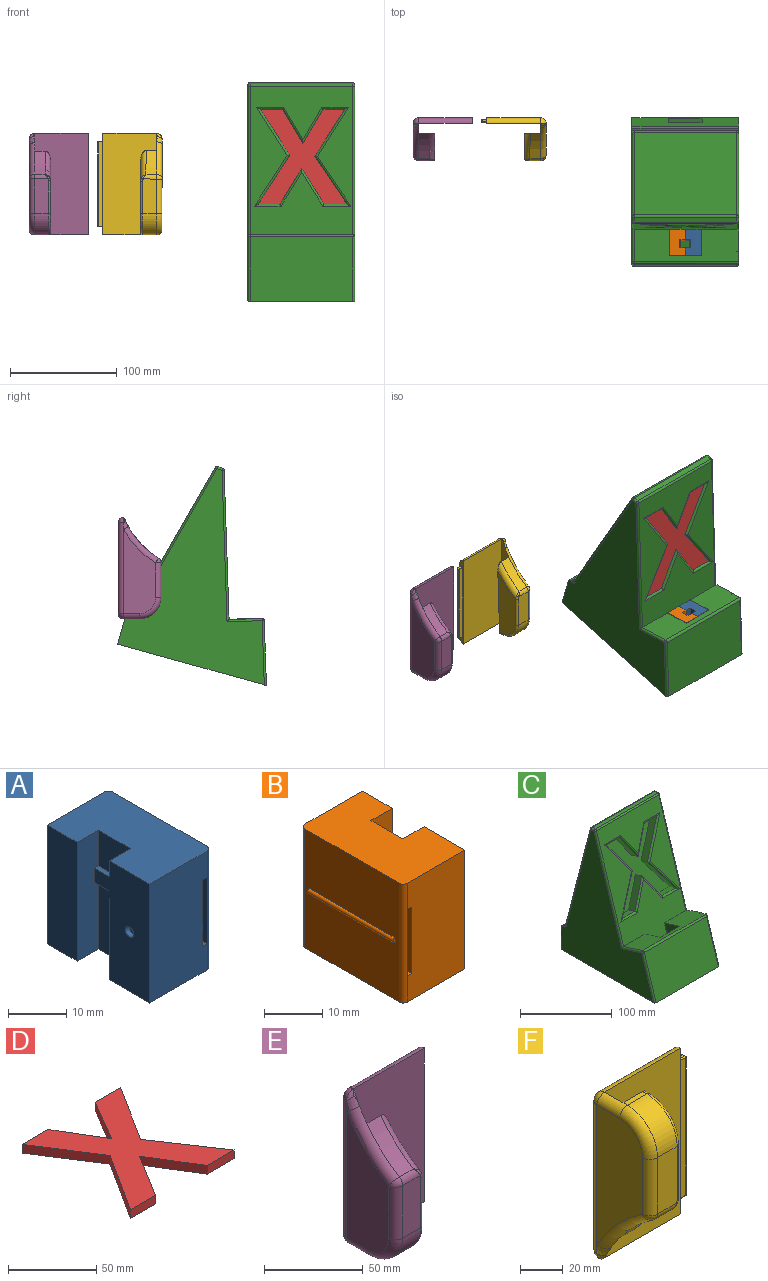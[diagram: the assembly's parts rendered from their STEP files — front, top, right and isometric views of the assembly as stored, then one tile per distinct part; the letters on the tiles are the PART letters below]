
ASSEMBLY  parts=6 mates=4
PART A: 25 faces, bbox 15.5x24.9x25 mm
  f0: plane 25x22.9mm, normal (1,0,0), area 551.6mm2, adj f6,f7,f20,f21,f22,f23,f24
  f1: plane 25x13.95mm, normal (0,1,0), area 334.7mm2, adj f6,f7,f8,f16,f18,f19,f24
  f2: plane 25x13.95mm, normal (0,-1,0), area 334.7mm2, adj f5,f6,f7,f16,f18,f19,f23
  f3: plane 7.75x7.5mm, normal (-1,0,0), area 58.1mm2, adj f4,f6,f9,f13
  f4: plane 25x5.17mm, normal (0,1,0), area 126.1mm2, adj f3,f5,f6,f7,f10,f13,f14,f15
  f5: plane 25x9.89mm, normal (-1,0,0), area 243.8mm2, adj f2,f4,f6,f7,f11
  f6: plane 24.9x14.95mm, normal (0,0,1), area 331.8mm2, adj f0,f1,f2,f3,f4,f5,f8,f9
  f7: plane 24.9x14.95mm, normal (0,0,-1), area 331.8mm2, adj f0,f1,f2,f4,f5,f8,f9,f10
  f8: plane 25x7.27mm, normal (-1,0,0), area 181.6mm2, adj f1,f6,f7,f9
  f9: plane 25x5.17mm, normal (0,-1,0), area 126.1mm2, adj f3,f6,f7,f8,f10,f13,f14,f15
  f10: plane 14.5x7.75mm, normal (-1,0,0), area 112.4mm2, adj f4,f7,f9,f14
  f11: cylinder r=1.03mm len=2.05mm, axis (-1,0,0), area 6.4mm2, adj f5,f12
  f12: plane 2.05x2.05mm, normal (-1,0,0), area 3.3mm2, adj f11
  f13: plane 7.75x1mm, normal (0,0,1), area 7.7mm2, adj f3,f4,f9,f15
  f14: plane 7.75x1mm, normal (0,0,-1), area 7.7mm2, adj f4,f9,f10,f15
  f15: plane 7.75x3mm, normal (-1,0,0), area 23.3mm2, adj f4,f9,f13,f14
  f16: plane 24.9x1mm, normal (0,0,-1), area 24.9mm2, adj f1,f2,f17,f19
  f17: plane 24.9x14mm, normal (-1,0,0), area 348.6mm2, adj f16,f18,f23,f24
  f18: plane 24.9x1mm, normal (0,0,1), area 24.9mm2, adj f1,f2,f17,f19
  f19: plane 24.9x14mm, normal (1,0,0), area 348.6mm2, adj f1,f2,f16,f18
  f20: plane 1x0.5mm, normal (0,-1,0), area 0.4mm2, adj f0,f21
  f21: cylinder r=0.5mm len=20.9mm, axis (0,1,0), area 32.8mm2, adj f0,f20,f22
  f22: plane 1x0.5mm, normal (0,1,0), area 0.4mm2, adj f0,f21
  f23: cylinder r=1mm len=25mm, axis (0,0,1), area 39.3mm2, adj f0,f2,f6,f7,f17
  f24: cylinder r=1mm len=25mm, axis (0,0,-1), area 39.3mm2, adj f0,f1,f6,f7,f17
PART B: 26 faces, bbox 16.5x24.9x25 mm
  f0: plane 25x13.95mm, normal (0,1,0), area 334.8mm2, adj f5,f6,f7,f18,f19,f20,f24
  f1: plane 25x13.95mm, normal (0,-1,0), area 334.8mm2, adj f4,f5,f6,f18,f19,f20,f25
  f2: plane 14.5x7.75mm, normal (1,0,0), area 112.4mm2, adj f3,f6,f9,f15
  f3: plane 25x5.17mm, normal (0,1,0), area 126.1mm2, adj f2,f4,f5,f6,f10,f14,f15,f16
  f4: plane 25x9.89mm, normal (1,0,0), area 244mm2, adj f1,f3,f5,f6,f11
  f5: plane 24.9x14.95mm, normal (0,0,1), area 331.8mm2, adj f0,f1,f3,f4,f7,f8,f9,f10
  f6: plane 24.9x14.95mm, normal (0,0,-1), area 331.8mm2, adj f0,f1,f2,f3,f4,f7,f8,f9
  f7: plane 25x7.27mm, normal (1,0,0), area 181.6mm2, adj f0,f5,f6,f9
  f8: plane 25x22.9mm, normal (-1,0,0), area 551.6mm2, adj f5,f6,f21,f22,f23,f24,f25
  f9: plane 25x5.17mm, normal (0,-1,0), area 126.1mm2, adj f2,f5,f6,f7,f10,f14,f15,f16
  f10: plane 7.75x7.5mm, normal (1,0,0), area 58.1mm2, adj f3,f5,f9,f14
  f11: cylinder r=1mm len=2mm, axis (-1,0,0), area 0.6mm2, adj f4,f13
  f12: plane 0.2x0.2mm, normal (1,0,0), area 0mm2, adj f13
  f13: torus R=0.1mm, axis (1,0,0), area 6mm2, adj f11,f12
  f14: plane 7.75x1mm, normal (0,0,1), area 7.8mm2, adj f3,f9,f10,f16
  f15: plane 7.75x1mm, normal (0,0,-1), area 7.8mm2, adj f2,f3,f9,f16
  f16: plane 7.75x3mm, normal (1,0,0), area 23.3mm2, adj f3,f9,f14,f15
  f17: plane 24.9x14mm, normal (1,0,0), area 348.6mm2, adj f18,f20,f24,f25
  f18: plane 24.9x1mm, normal (0,0,-1), area 24.9mm2, adj f0,f1,f17,f19
  f19: plane 24.9x14mm, normal (-1,0,0), area 348.6mm2, adj f0,f1,f18,f20
  f20: plane 24.9x1mm, normal (0,0,1), area 24.9mm2, adj f0,f1,f17,f19
  f21: plane 1x0.5mm, normal (0,-1,0), area 0.4mm2, adj f8,f23
  f22: plane 1x0.5mm, normal (0,1,0), area 0.4mm2, adj f8,f23
  f23: cylinder r=0.5mm len=20.9mm, axis (0,1,0), area 32.8mm2, adj f8,f21,f22
  f24: cylinder r=1mm len=25mm, axis (0,0,-1), area 39.3mm2, adj f0,f5,f6,f8,f17
  f25: cylinder r=1mm len=25mm, axis (0,0,1), area 39.3mm2, adj f1,f5,f6,f8,f17
PART C: 74 faces, bbox 104.8x145.3x186.4 mm
  f0: plane 44.02x37.32mm, normal (1,0,0), area 931.5mm2, adj f6,f9,f54,f58,f61,f62,f71,f72
  f1: plane 44.02x37.32mm, normal (-1,0,0), area 931.5mm2, adj f6,f9,f54,f58,f61,f62,f68,f69
  f2: plane 100x30.22mm, normal (0,1,0), area 2531.6mm2, adj f3,f5,f8,f38,f54,f55,f56,f57
  f3: plane 183.83x143.2mm, normal (-1,0,0), area 12324.4mm2, adj f2,f5,f10,f26,f30,f31,f38,f51
  f4: plane 2.36x2.26mm, normal (0,0,1), area 0.9mm2, adj f8,f25,f59
  f5: plane 144.72x100.26mm, normal (0,0,-1), area 14444.2mm2, adj f2,f3,f8,f60,f63,f67
  f6: plane 165.85x96mm, normal (0,-0.95,0.3), area 10214.6mm2, adj f0,f1,f9,f26,f28,f29,f39,f40
  f7: plane 96x4.78mm, normal (0,0,1), area 459.1mm2, adj f29,f30,f34,f35
  f8: plane 183.83x143.2mm, normal (1,0,0), area 12324.9mm2, adj f2,f4,f5,f9,f10,f25,f28,f34
  f9: plane 98x31.34mm, normal (0,0.3,0.95), area 2272.5mm2, adj f0,f1,f6,f8,f25,f28,f59,f61
  f10: plane 100x2mm, normal (0,0,1), area 145.2mm2, adj f3,f8,f38,f51,f52,f53
  f11: plane 149.78x96mm, normal (0,0.97,0.25), area 14844.8mm2, adj f31,f35,f37,f52
  f12: plane 21.45x9.54mm, normal (0,0.3,0.95), area 214.5mm2, adj f13,f23,f24,f46
  f13: plane 45.62x29.95mm, normal (-0.83,-0.17,-0.53), area 537.8mm2, adj f12,f14,f24,f44
  f14: plane 44.93x27.82mm, normal (-0.85,0.16,0.51), area 520.2mm2, adj f13,f15,f24,f42
  f15: plane 20.23x9.54mm, normal (0,-0.3,-0.95), area 202.3mm2, adj f14,f16,f24,f40
  f16: plane 33.42x19.08mm, normal (0.86,-0.15,-0.48), area 369.9mm2, adj f15,f17,f24,f39
  f17: plane 33.42x19.09mm, normal (-0.86,-0.15,-0.49), area 371.7mm2, adj f16,f18,f24,f41
  f18: plane 20.74x9.54mm, normal (0,-0.3,-0.95), area 207.4mm2, adj f17,f19,f24,f43
  f19: plane 43.95x27.53mm, normal (0.84,0.16,0.52), area 509.9mm2, adj f18,f20,f24,f45
  f20: plane 46.6x29.41mm, normal (0.84,-0.16,-0.52), area 543.5mm2, adj f19,f21,f24,f47
  f21: plane 20.14x9.54mm, normal (0,0.3,0.95), area 201.4mm2, adj f20,f22,f24,f49
  f22: plane 34.98x20.6mm, normal (-0.85,0.16,0.5), area 393.4mm2, adj f21,f23,f24,f50
  f23: plane 34.98x20.62mm, normal (0.85,0.16,0.5), area 393.5mm2, adj f12,f22,f24,f48
  f24: plane 84.57x82.81mm, normal (0,-0.95,0.3), area 3327.7mm2, adj f12,f13,f14,f15,f16,f17,f18,f19
  f25: cylinder r=2mm len=32mm, axis (0,-0.3,-0.95), area 102.4mm2, adj f4,f8,f9,f59
  f26: cylinder r=2mm len=136.11mm, axis (0,-0.3,-0.95), area 443mm2, adj f3,f6,f27,f64
  f27: sphere r=2mm, area 5.3mm2, adj f26,f29,f30
  f28: cylinder r=2mm len=134.2mm, axis (0,-0.3,-0.95), area 439.9mm2, adj f6,f8,f9,f32
  f29: cylinder r=2mm len=96mm, axis (-1,0,0), area 243.2mm2, adj f6,f7,f27,f32
  f30: cylinder r=2mm len=4.78mm, axis (0,1,0), area 15mm2, adj f3,f7,f27,f33
  f31: cylinder r=2mm len=150.27mm, axis (0,-0.25,0.97), area 484.2mm2, adj f3,f11,f33,f51
  f32: sphere r=2mm, area 2.8mm2, adj f28,f29,f34
  f33: sphere r=2mm, area 9.5mm2, adj f30,f31,f35
  f34: cylinder r=2mm len=4.78mm, axis (0,-1,0), area 15mm2, adj f7,f8,f32,f36
  f35: cylinder r=2mm len=96mm, axis (1,0,0), area 253.3mm2, adj f7,f11,f33,f36
  f36: sphere r=2mm, area 7.2mm2, adj f34,f35,f37
  f37: cylinder r=2mm len=150.27mm, axis (0,-0.25,0.97), area 484.2mm2, adj f8,f11,f36,f53
  f38: cylinder r=2mm len=100mm, axis (1,0,0), area 314.2mm2, adj f2,f3,f8,f10
  f39: cylinder r=2mm len=32.94mm, axis (0.51,0.26,0.82), area 112.7mm2, adj f6,f16,f40,f41
  f40: cylinder r=2mm len=25.01mm, axis (1,0,0), area 71.1mm2, adj f6,f15,f39,f42
  f41: cylinder r=2mm len=32.94mm, axis (0.51,-0.26,-0.82), area 113.2mm2, adj f6,f17,f39,f43
  f42: cylinder r=2mm len=45.46mm, axis (-0.53,-0.25,-0.81), area 167.1mm2, adj f6,f14,f40,f44
  f43: cylinder r=2mm len=25.53mm, axis (1,0,0), area 72.7mm2, adj f6,f18,f41,f45
  f44: cylinder r=2mm len=47.26mm, axis (0.56,-0.25,-0.79), area 172.8mm2, adj f6,f13,f42,f46
  f45: cylinder r=2mm len=44.49mm, axis (-0.54,0.25,0.8), area 163.9mm2, adj f6,f19,f43,f47
  f46: cylinder r=2mm len=26.32mm, axis (-1,0,0), area 75mm2, adj f6,f12,f44,f48
  f47: cylinder r=2mm len=48.18mm, axis (0.54,0.25,0.8), area 174.5mm2, adj f6,f20,f45,f49
  f48: cylinder r=2mm len=33.46mm, axis (-0.52,0.25,0.81), area 120.3mm2, adj f6,f23,f46,f50
  f49: cylinder r=2mm len=24.92mm, axis (-1,0,0), area 70.8mm2, adj f6,f21,f47,f50
  f50: cylinder r=2mm len=33.46mm, axis (-0.52,-0.25,-0.81), area 120.3mm2, adj f6,f22,f48,f49
  f51: bspline ~4.85x4.17mm, area 7.7mm2, adj f3,f10,f31,f52
  f52: cylinder r=2mm len=96mm, axis (1,0,0), area 253.3mm2, adj f10,f11,f51,f53
  f53: bspline ~4.85x4.7mm, area 7.7mm2, adj f8,f10,f37,f52
  f54: plane 126.89x31.57mm, normal (0,0,-1), area 3334mm2, adj f0,f1,f2,f6,f55,f57,f58
  f55: plane 131.75x15.53mm, normal (-1,0,0), area 2008.1mm2, adj f2,f54,f56,f58
  f56: plane 131.75x31.57mm, normal (0,0,1), area 4160.1mm2, adj f2,f55,f57,f58
  f57: plane 131.75x15.53mm, normal (1,0,0), area 2008.1mm2, adj f2,f54,f56,f58
  f58: plane 31.57x15.53mm, normal (0,0.95,-0.3), area 379.1mm2, adj f0,f1,f54,f55,f56,f57,f62
  f59: plane 31.4x9.85mm, normal (0,0.95,-0.3), area 65.8mm2, adj f4,f8,f9,f25
  f60: plane 96x57.92mm, normal (0,-0.95,0.3), area 5827.3mm2, adj f5,f63,f66,f67
  f61: plane 42.94x30mm, normal (0,0.95,-0.3), area 1350mm2, adj f0,f1,f9,f62
  f62: plane 30x3.45mm, normal (0,0.3,0.95), area 108.5mm2, adj f0,f1,f58,f61
  f63: cylinder r=2mm len=58.52mm, axis (0,-0.3,-0.95), area 189.7mm2, adj f3,f5,f60,f65
  f64: cylinder r=2mm len=31.94mm, axis (0,-0.95,0.3), area 100mm2, adj f3,f9,f26,f65
  f65: sphere r=2mm, area 6.6mm2, adj f63,f64,f66
  f66: cylinder r=2mm len=98mm, axis (1,0,0), area 305.6mm2, adj f9,f60,f65,f67
  f67: cylinder r=2mm len=60.43mm, axis (0,0.3,0.95), area 192.9mm2, adj f5,f8,f60,f66
  f68: plane 1.05x0.55mm, normal (0,-0.95,0.3), area 0.5mm2, adj f1,f69
  f69: cylinder r=0.55mm len=22.7mm, axis (0,-0.95,0.3), area 40.5mm2, adj f1,f68,f70
  f70: plane 1.05x0.55mm, normal (0,0.95,-0.3), area 0.5mm2, adj f1,f69
  f71: plane 1.05x0.55mm, normal (0,-0.95,0.3), area 0.5mm2, adj f0,f72
  f72: cylinder r=0.55mm len=22.7mm, axis (0,-0.95,0.3), area 40.5mm2, adj f0,f71,f73
  f73: plane 1.05x0.55mm, normal (0,0.95,-0.3), area 0.5mm2, adj f0,f72
PART D: 14 faces, bbox 82.8x88.6x6 mm
  f0: plane 21.45x6mm, normal (0,-1,0), area 128.7mm2, adj f1,f11,f12,f13
  f1: plane 44.67x29.95mm, normal (0.83,0.56,0), area 322.7mm2, adj f0,f2,f12,f13
  f2: plane 43.96x27.82mm, normal (0.85,-0.53,0), area 312.1mm2, adj f1,f3,f12,f13
  f3: plane 20.23x6mm, normal (0,1,0), area 121.4mm2, adj f2,f4,f12,f13
  f4: plane 31.89x18.74mm, normal (-0.86,0.51,0), area 221.9mm2, adj f3,f5,f12,f13
  f5: plane 31.89x19.09mm, normal (0.86,0.51,0), area 223mm2, adj f4,f6,f12,f13
  f6: plane 20.74x6mm, normal (0,1,0), area 124.4mm2, adj f5,f7,f12,f13
  f7: plane 42.93x27.53mm, normal (-0.84,-0.54,0), area 306mm2, adj f6,f8,f12,f13
  f8: plane 45.7x29.41mm, normal (-0.84,0.54,0), area 326.1mm2, adj f7,f9,f12,f13
  f9: plane 20.14x6mm, normal (0,-1,0), area 120.8mm2, adj f8,f10,f12,f13
  f10: plane 33.52x20.6mm, normal (0.85,-0.52,0), area 236.1mm2, adj f9,f11,f12,f13
  f11: plane 33.52x20.62mm, normal (-0.85,-0.52,0), area 236.1mm2, adj f0,f10,f12,f13
  f12: plane 88.63x82.81mm, normal (0,0,1), area 3327.7mm2, adj f0,f1,f2,f3,f4,f5,f6,f7
  f13: plane 88.63x82.81mm, normal (0,0,-1), area 3327.7mm2, adj f0,f1,f2,f3,f4,f5,f6,f7
PART E: 36 faces, bbox 55.7x46.3x96.7 mm
  f0: cylinder r=82.71mm len=8.24mm, axis (-1,0,0), area 6.6mm2, adj f9,f34,f35
  f1: plane 95x5mm, normal (1,0,0), area 224.3mm2, adj f3,f4,f10,f11,f12,f13,f16,f18
  f2: plane 67.82x23.23mm, normal (1,0,0), area 1177.3mm2, adj f8,f24,f25,f26,f28
  f3: plane 95x50.5mm, normal (0,-1,0), area 4797.5mm2, adj f1,f9,f16,f18
  f4: plane 85x50.5mm, normal (0,1,0), area 4292.5mm2, adj f1,f16,f18,f19
  f5: plane 78.75x30mm, normal (-1,0,0), area 1766mm2, adj f19,f21,f22,f23,f33
  f6: plane 32.46x13mm, normal (0,-1,0), area 421.8mm2, adj f15,f22,f24,f29,f31
  f7: plane 13x2.8mm, normal (0,0,-1), area 36.4mm2, adj f8,f15,f21,f26
  f8: plane 78.27x15.03mm, normal (0,1,-0.03), area 1164.1mm2, adj f2,f7,f9,f26,f27,f28
  f9: plane 95x12.2mm, normal (1,0,0), area 920.8mm2, adj f0,f3,f8,f21,f33,f35
  f10: plane 5x3mm, normal (0,0,-1), area 15mm2, adj f1,f11,f13,f14
  f11: plane 80x5mm, normal (0,1,0), area 400mm2, adj f1,f10,f12,f14
  f12: plane 5x3mm, normal (0,0,1), area 15mm2, adj f1,f11,f13,f14
  f13: plane 80x5mm, normal (0,-1,0), area 400mm2, adj f1,f10,f12,f14
  f14: plane 80x3mm, normal (1,0,0), area 240mm2, adj f10,f11,f12,f13
  f15: cylinder r=20mm len=20mm, axis (1,0,0), area 408.4mm2, adj f6,f7,f23,f25
  f16: cylinder r=5mm len=50.5mm, axis (1,0,0), area 396.6mm2, adj f1,f3,f4,f17
  f17: sphere r=5mm, area 39.3mm2, adj f16,f19,f35
  f18: cylinder r=5mm len=50.5mm, axis (-1,0,0), area 396.6mm2, adj f1,f3,f4,f20
  f19: cylinder r=5mm len=85mm, axis (0,0,-1), area 667.6mm2, adj f4,f5,f17,f20,f34
  f20: sphere r=5mm, area 39.3mm2, adj f18,f19,f21
  f21: cylinder r=5mm len=15mm, axis (0,-1,0), area 117.8mm2, adj f5,f7,f9,f20,f23
  f22: cylinder r=5mm len=32.46mm, axis (0,0,1), area 255mm2, adj f5,f6,f23,f32
  f23: torus R=15mm, axis (-1,0,0), area 224.3mm2, adj f5,f15,f21,f22
  f24: cylinder r=2mm len=30.68mm, axis (0,0,1), area 96.4mm2, adj f2,f6,f25,f29
  f25: torus R=18mm, axis (1,0,0), area 95.1mm2, adj f2,f15,f24,f26
  f26: cylinder r=2mm len=2.87mm, axis (0,1,0), area 8.9mm2, adj f2,f7,f8,f25
  f27: cylinder r=82.71mm len=23.16mm, axis (-1,0,0), area 318.2mm2, adj f8,f28,f31,f33
  f28: torus R=87.71mm, axis (1,0,0), area 249.6mm2, adj f2,f8,f27,f29,f30
  f29: bspline ~4.19x2.6mm, area 7mm2, adj f6,f24,f28,f30
  f30: bspline ~5.07x4.66mm, area 5.4mm2, adj f28,f29,f31
  f31: cylinder r=5mm len=12.57mm, axis (-1,0,0), area 57.2mm2, adj f6,f27,f30,f32
  f32: sphere r=5mm, area 25.4mm2, adj f22,f31,f33
  f33: torus R=87.71mm, axis (-1,0,0), area 331.5mm2, adj f5,f9,f27,f32,f34
  f34: bspline ~9.39x5.18mm, area 37.5mm2, adj f0,f19,f33,f35
  f35: bspline ~5.61x5.14mm, area 12mm2, adj f0,f9,f17,f34
PART F: 48 faces, bbox 60.6x46.7x96.7 mm
  f0: cylinder r=87.71mm len=6.43mm, axis (-1,0,0), area 3.1mm2, adj f9,f46,f47
  f1: plane 13x2.8mm, normal (0,0,1), area 36.4mm2, adj f8,f27,f28,f34
  f2: plane 95x50.5mm, normal (0,-1,0), area 4797.5mm2, adj f3,f9,f35,f37
  f3: plane 95x5mm, normal (1,0,0), area 232.8mm2, adj f2,f4,f10,f11,f12,f13,f15,f17
  f4: plane 85x50.5mm, normal (0,1,0), area 4292.5mm2, adj f3,f29,f35,f37
  f5: plane 79.58x30mm, normal (-1,0,0), area 1777.9mm2, adj f28,f29,f30,f31,f45
  f6: plane 32.37x13mm, normal (0,-1,0), area 420.5mm2, adj f27,f31,f32,f40,f43
  f7: plane 68.42x23.25mm, normal (1,0,0), area 1181.8mm2, adj f8,f32,f33,f34,f41
  f8: plane 79.01x15.03mm, normal (0,1,0.03), area 1175mm2, adj f1,f7,f9,f34,f39,f41
  f9: plane 95x12.2mm, normal (1,0,0), area 928.2mm2, adj f0,f2,f8,f28,f45,f47
  f10: plane 4.3x1.9mm, normal (0,0,-1), area 8.2mm2, adj f3,f17,f23,f26
  f11: plane 78.9x4.3mm, normal (0,1,0), area 339.3mm2, adj f3,f20,f24,f26
  f12: plane 4.3x1.9mm, normal (0,0,1), area 8.2mm2, adj f3,f15,f19,f20
  f13: plane 78.9x4.3mm, normal (0,-1,0), area 339.3mm2, adj f3,f15,f17,f18
  f14: plane 78.9x1.9mm, normal (1,0,0), area 149.9mm2, adj f18,f19,f23,f24
  f15: cylinder r=0.5mm len=4.3mm, axis (1,0,0), area 3.4mm2, adj f3,f12,f13,f16
  f16: sphere r=0.5mm, area 0.4mm2, adj f15,f18,f19
  f17: cylinder r=0.5mm len=4.3mm, axis (-1,0,0), area 3.4mm2, adj f3,f10,f13,f21
  f18: cylinder r=0.5mm len=78.9mm, axis (0,0,1), area 62mm2, adj f13,f14,f16,f21
  f19: cylinder r=0.5mm len=1.9mm, axis (0,1,0), area 1.5mm2, adj f12,f14,f16,f22
  f20: cylinder r=0.5mm len=4.3mm, axis (-1,0,0), area 3.4mm2, adj f3,f11,f12,f22
  f21: sphere r=0.5mm, area 0.4mm2, adj f17,f18,f23
  f22: sphere r=0.5mm, area 0.2mm2, adj f19,f20,f24
  f23: cylinder r=0.5mm len=1.9mm, axis (0,-1,0), area 1.5mm2, adj f10,f14,f21,f25
  f24: cylinder r=0.5mm len=78.9mm, axis (0,0,-1), area 62mm2, adj f11,f14,f22,f25
  f25: sphere r=0.5mm, area 0.3mm2, adj f23,f24,f26
  f26: cylinder r=0.5mm len=4.3mm, axis (1,0,0), area 3.4mm2, adj f3,f10,f11,f25
  f27: cylinder r=20mm len=20mm, axis (-1,0,0), area 408.4mm2, adj f1,f6,f30,f33
  f28: cylinder r=5mm len=15mm, axis (0,1,0), area 117.8mm2, adj f1,f5,f9,f30,f38
  f29: cylinder r=5mm len=85mm, axis (0,0,-1), area 667.6mm2, adj f4,f5,f36,f38,f46
  f30: torus R=15mm, axis (-1,0,0), area 224.3mm2, adj f5,f27,f28,f31
  f31: cylinder r=5mm len=32.37mm, axis (0,0,1), area 254.2mm2, adj f5,f6,f30,f44
  f32: cylinder r=2mm len=30.48mm, axis (0,0,1), area 95.7mm2, adj f6,f7,f33,f40
  f33: torus R=18mm, axis (1,0,0), area 95.1mm2, adj f7,f27,f32,f34
  f34: cylinder r=2mm len=2.87mm, axis (0,-1,0), area 8.9mm2, adj f1,f7,f8,f33
  f35: cylinder r=5mm len=50.5mm, axis (-1,0,0), area 396.6mm2, adj f2,f3,f4,f36
  f36: sphere r=5mm, area 39.3mm2, adj f29,f35,f47
  f37: cylinder r=5mm len=50.5mm, axis (1,0,0), area 396.6mm2, adj f2,f3,f4,f38
  f38: sphere r=5mm, area 39.3mm2, adj f28,f29,f37
  f39: cylinder r=87.71mm len=23.29mm, axis (-1,0,0), area 325.2mm2, adj f8,f41,f43,f45
  f40: bspline ~4.05x2.76mm, area 7.3mm2, adj f6,f32,f41,f42
  f41: torus R=92.71mm, axis (1,0,0), area 254.6mm2, adj f7,f8,f39,f40,f42
  f42: bspline ~5.01x4.61mm, area 5.1mm2, adj f40,f41,f43
  f43: cylinder r=5mm len=12.53mm, axis (-1,0,0), area 55.7mm2, adj f6,f39,f42,f44
  f44: sphere r=5mm, area 24.7mm2, adj f31,f43,f45
  f45: torus R=92.71mm, axis (-1,0,0), area 337.1mm2, adj f5,f9,f39,f44,f46
  f46: bspline ~8.88x5.29mm, area 33.6mm2, adj f0,f29,f45,f47
  f47: bspline ~5.48x5.42mm, area 14.8mm2, adj f0,f9,f36,f46
PLACE A rot(axis=(1,0,0),178.1deg) t=(-2.32,96.09,-82.06)mm
PLACE B rot(axis=(1,0,0),178.1deg) t=(-72.29,99.69,-82.18)mm
PLACE C rot(axis=(1,0,0),15.5deg) t=(-73.56,129.73,-105.37)mm fixed
PLACE D rot(axis=(1,0,0),88.1deg) t=(-73.78,123.83,-106.08)mm
PLACE E t=(-322.43,200.37,-82.42)mm
PLACE F rot(axis=(0,-1,0),179.9deg) t=(-257.39,199.21,12.54)mm
MATE slider B.f6 <-> C.f9  axis (0,0.03,1) through (-110.56,104.11,-82.33)mm
MATE pin_slot F.f13 <-> E.f11  axis (0,-1,0) through (-283.58,216.37,-34.92)mm
MATE fastened B.f13 <-> A.f11  axis (1,0,0) through (-95.61,111.2,-95.07)mm
MATE fastened C.f21 <-> D.f9  axis (0,0.03,1) through (-125.75,119.58,-53.58)mm
